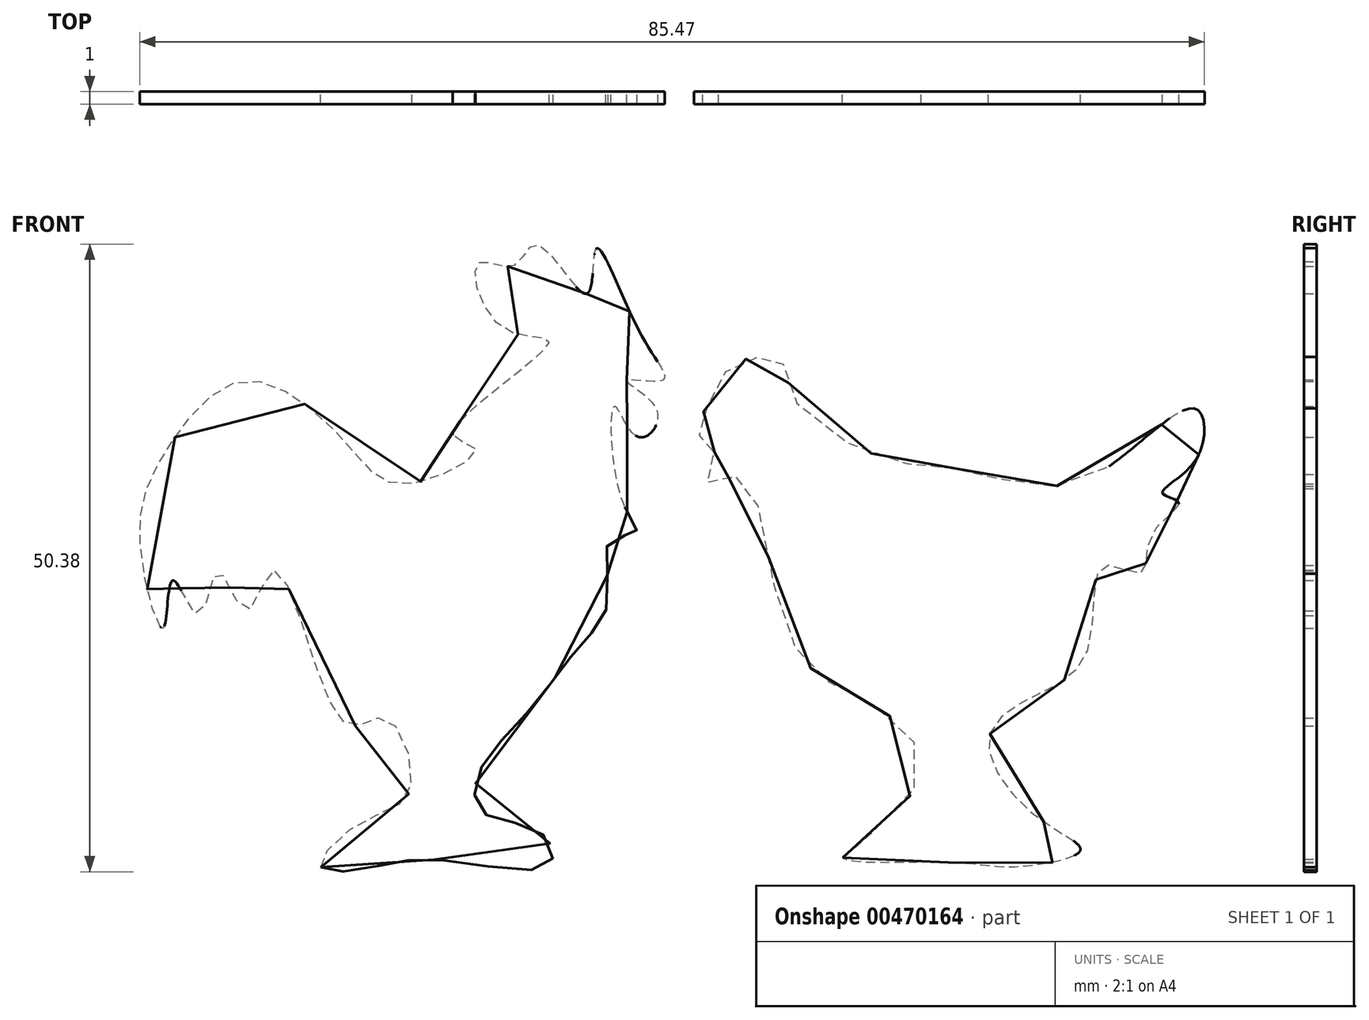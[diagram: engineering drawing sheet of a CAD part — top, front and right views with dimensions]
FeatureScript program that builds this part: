
annotation { "Feature Type Name" : "Feature", "Feature Type Description" : "" }
export const myFeature = defineFeature(function(context is Context, id is Id, definition is map)
    precondition{}
    {
        {
            var Q0;
            Q0=qCreatedBy(makeId("Front.planeOp"),FACE);
            var sketch = newSketch(context, id + "F0", { "sketchPlane" : qUnion([Q0])});
            skFitSpline(sketch, "E0", {"points": [v(-53.57, 11.41) * mm, v(-50.36, 15) * mm, v(-46.4, 17.64) * mm, v(-48.29, 23.3) * mm, v(-50.93, 22.73) * mm, v(-53.95, 27.44) * mm, v(-57.53, 35.18) * mm, v(-59.6, 31.97) * mm, v(-61.87, 35.18) * mm, v(-63.38, 31.6) * mm, v(-65.45, 34.42) * mm, v(-66.2, 30.65) * mm, v(-68.1, 37.25) * mm, v(-66.02, 44.8) * mm, v(-59.6, 50.46) * mm, v(-51.5, 45.36) * mm, v(-46.78, 42.16) * mm, v(-41.12, 44.99) * mm, v(-43, 46.12) * mm, v(-35.27, 53.47) * mm, v(-38.86, 54.6) * mm, v(-40.93, 59.89) * mm, v(-38.1, 59.7) * mm, v(-36.22, 61.4) * mm, v(-32.25, 57.44) * mm, v(-31.5, 61.02) * mm, v(-27.73, 53.85) * mm, v(-26.22, 50.46) * mm, v(-29.05, 50.46) * mm, v(-26.6, 48) * mm, v(-28.1, 45.93) * mm, v(-30, 48.38) * mm, v(-29.43, 40.84) * mm, v(-28.3, 38.2) * mm, v(-30.37, 37.63) * mm, v(-30.56, 32.73) * mm, v(-32.82, 29.14) * mm, v(-36.97, 23.86) * mm, v(-40.93, 18.96) * mm, v(-40.55, 15.75) * mm, v(-36.03, 14.24) * mm, v(-35.27, 11.6) * mm, v(-43.95, 11.98) * mm, v(-49.42, 11.41) * mm, v(-53.57, 11.41) * mm]});
            skSolve(sketch);
        }
        {
            var Q0;
            Q0 = qSketchRegion(id + "F0", true);
            extrude(context, id + "F1", {"entities" : qUnion([Q0]), "depth" : 1 * mm, "offsetDistance" : 25 * mm});
        }
        {
            var Q0;
            Q0=qCreatedBy(makeId("Front.planeOp"),FACE);
            var sketch = newSketch(context, id + "F2", { "sketchPlane" : qUnion([Q0])});
            skFitSpline(sketch, "E1", {"points": [v(-11.7, 12.17) * mm, v(-8.3, 15) * mm, v(-5.47, 20.09) * mm, v(-9.24, 24.43) * mm, v(-13.96, 27.07) * mm, v(-17.16, 33.86) * mm, v(-19.8, 42.91) * mm, v(-21.88, 41.78) * mm, v(-22.82, 44.04) * mm, v(-21.7, 44.99) * mm, v(-23.58, 46.5) * mm, v(-22.26, 48.76) * mm, v(-20.75, 51.59) * mm, v(-18.1, 52.34) * mm, v(-16.6, 51.97) * mm, v(-15.47, 48.76) * mm, v(-7.73, 44.04) * mm, v(-3.2, 43.48) * mm, v(3.02, 42.16) * mm, v(9.24, 43.29) * mm, v(16.6, 48.2) * mm, v(16.6, 44.04) * mm, v(13.96, 41.4) * mm, v(15.28, 40.65) * mm, v(13.01, 38) * mm, v(12.26, 34.99) * mm, v(9.24, 35.56) * mm, v(7.92, 28.76) * mm, v(3.4, 25) * mm, v(0, 21.6) * mm, v(3.96, 15.37) * mm, v(7.36, 12.73) * mm, v(2.07, 11.41) * mm, v(-3.2, 11.79) * mm, v(-11.7, 12.17) * mm]});
            skSolve(sketch);
        }
        {
            var Q0;
            Q0 = qSketchRegion(id + "F2", true);
            extrude(context, id + "F3", {"entities" : qUnion([Q0]), "depth" : 1 * mm, "offsetDistance" : 25 * mm});
        }
    });
